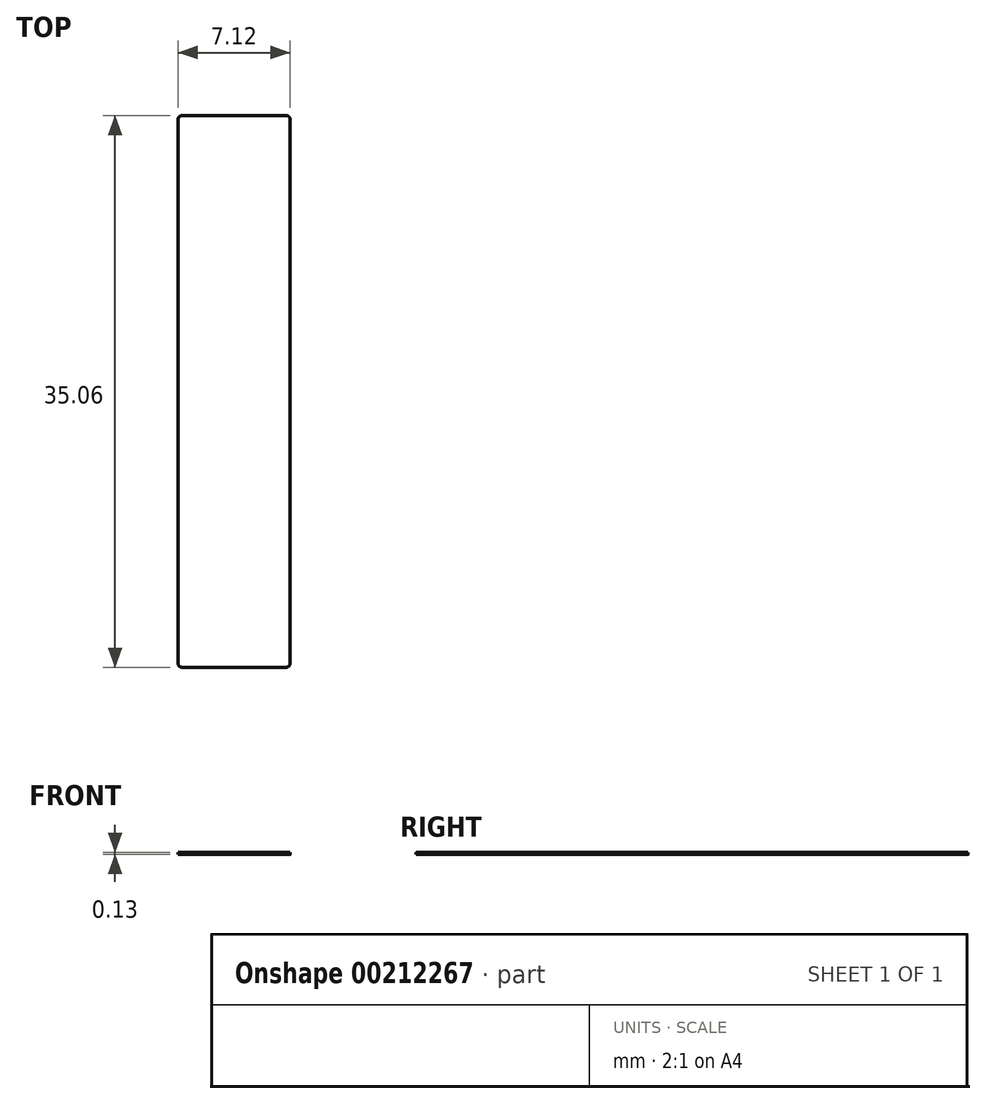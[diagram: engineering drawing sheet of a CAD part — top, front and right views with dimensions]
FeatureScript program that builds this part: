
annotation { "Feature Type Name" : "Feature", "Feature Type Description" : "" }
export const myFeature = defineFeature(function(context is Context, id is Id, definition is map)
    precondition{}
    {
        {
            var Q0;
            Q0=qCreatedBy(makeId("Top.planeOp"),FACE);
            var sketch = newSketch(context, id + "F0", { "sketchPlane" : qUnion([Q0])});
            skLineSegment(sketch, "E0.bottom", {"start": v(3.3, -17.53) * mm, "end": v(-3.3, -17.53) * mm});
            skLineSegment(sketch, "E0.top", {"start": v(3.3, 17.53) * mm, "end": v(-3.3, 17.53) * mm});
            skLineSegment(sketch, "E0.left", {"start": v(3.56, -17.27) * mm, "end": v(3.56, 17.27) * mm});
            skLineSegment(sketch, "E0.right", {"start": v(-3.56, -17.27) * mm, "end": v(-3.56, 17.27) * mm});
            skPoint(sketch, "E0.middle", {"position": v(0, 0) * mm});
            skPoint(sketch, "E1.visualSharp", {"position": v(-3.56, 17.53) * mm});
            skArc(sketch, "E1.filletArc", {"start": v(-3.3, 17.53) * mm, "mid": v(-3.48, 17.45) * mm, "end": v(-3.56, 17.27) * mm});
            skPoint(sketch, "E2.visualSharp", {"position": v(3.56, 17.53) * mm});
            skArc(sketch, "E2.filletArc", {"start": v(3.56, 17.27) * mm, "mid": v(3.48, 17.45) * mm, "end": v(3.3, 17.53) * mm});
            skPoint(sketch, "E3.visualSharp", {"position": v(3.56, -17.53) * mm});
            skArc(sketch, "E3.filletArc", {"start": v(3.3, -17.53) * mm, "mid": v(3.48, -17.45) * mm, "end": v(3.56, -17.27) * mm});
            skPoint(sketch, "E4.visualSharp", {"position": v(-3.56, -17.53) * mm});
            skArc(sketch, "E4.filletArc", {"start": v(-3.56, -17.27) * mm, "mid": v(-3.48, -17.45) * mm, "end": v(-3.3, -17.53) * mm});
            skSolve(sketch);
        }
        {
            var Q0;
            Q0 = qSketchRegion(id + "F0", true);
            extrude(context, id + "F1", {"entities" : qUnion([Q0]), "depth" : 0.13 * mm});
        }
    });
